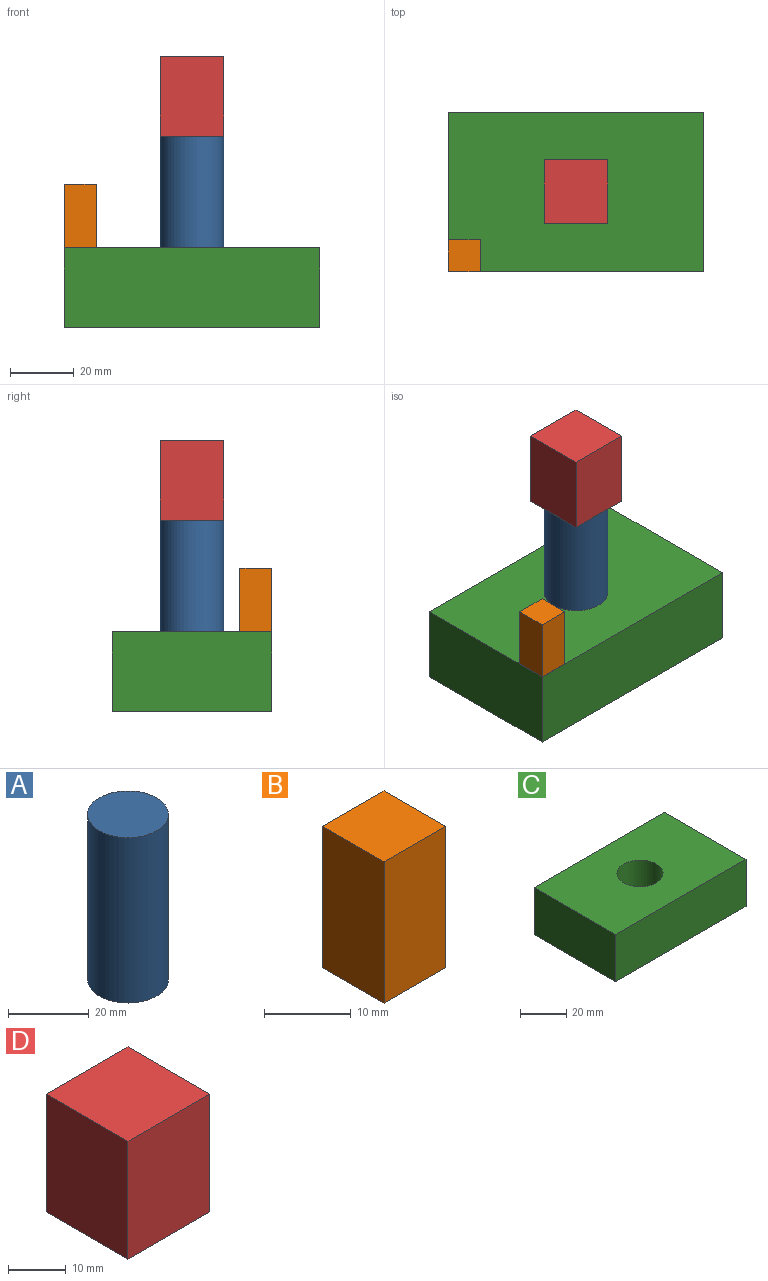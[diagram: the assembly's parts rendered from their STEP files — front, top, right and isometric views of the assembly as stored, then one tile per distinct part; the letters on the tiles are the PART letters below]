
ASSEMBLY  parts=4 mates=3
PART A: 3 faces, bbox 20x20x50 mm
  f0: cylinder r=10mm len=50mm, axis (0,0,1), area 3141.6mm2, adj f1,f2
  f1: plane 20x20mm, normal (0,0,-1), area 314.2mm2, adj f0
  f2: plane 20x20mm, normal (0,0,1), area 314.2mm2, adj f0
PART B: 6 faces, bbox 10x10x20 mm
  f0: plane 20x10mm, normal (0,1,0), area 200mm2, adj f1,f3,f4,f5
  f1: plane 20x10mm, normal (-1,0,0), area 200mm2, adj f0,f2,f4,f5
  f2: plane 20x10mm, normal (0,-1,0), area 200mm2, adj f1,f3,f4,f5
  f3: plane 20x10mm, normal (1,0,0), area 200mm2, adj f0,f2,f4,f5
  f4: plane 10x10mm, normal (0,0,1), area 100mm2, adj f0,f1,f2,f3
  f5: plane 10x10mm, normal (0,0,-1), area 100mm2, adj f0,f1,f2,f3
PART C: 7 faces, bbox 80x50x25 mm
  f0: plane 80x25mm, normal (0,1,0), area 2000mm2, adj f1,f4,f5,f6
  f1: plane 50x25mm, normal (-1,0,0), area 1250mm2, adj f0,f2,f5,f6
  f2: plane 80x25mm, normal (0,-1,0), area 2000mm2, adj f1,f4,f5,f6
  f3: cylinder r=10mm len=25mm, axis (0,0,1), area 1570.8mm2, adj f5,f6
  f4: plane 50x25mm, normal (1,0,0), area 1250mm2, adj f0,f2,f5,f6
  f5: plane 80x50mm, normal (0,0,-1), area 3685.8mm2, adj f0,f1,f2,f3,f4
  f6: plane 80x50mm, normal (0,0,1), area 3685.8mm2, adj f0,f1,f2,f3,f4
PART D: 6 faces, bbox 20x20x25 mm
  f0: plane 25x20mm, normal (0,-1,0), area 500mm2, adj f1,f3,f4,f5
  f1: plane 25x20mm, normal (1,0,0), area 500mm2, adj f0,f2,f4,f5
  f2: plane 25x20mm, normal (0,1,0), area 500mm2, adj f1,f3,f4,f5
  f3: plane 25x20mm, normal (-1,0,0), area 500mm2, adj f0,f2,f4,f5
  f4: plane 20x20mm, normal (0,0,1), area 400mm2, adj f0,f1,f2,f3
  f5: plane 20x20mm, normal (0,0,-1), area 400mm2, adj f0,f1,f2,f3
PLACE A rot(axis=(0,0,1),180deg) t=(-92.79,-22.94,77.44)mm
PLACE B t=(-13.69,-43.07,42.44)mm
PLACE C rot(axis=(1,0,0),180deg) t=(-41.79,-83.08,17.44)mm
PLACE D t=(-90.81,-139.95,77.44)mm fixed
MATE cylindrical C.f3 <-> A.f0  axis (0,0,-1) through (-41.79,-83.08,17.44)mm
MATE fastened B.f5 <-> C.f5  axis (0,0,1) through (-81.79,-108.08,42.44)mm
MATE fastened D.f5 <-> A.f0  axis (0,0,-1) through (-41.79,-83.08,77.44)mm
